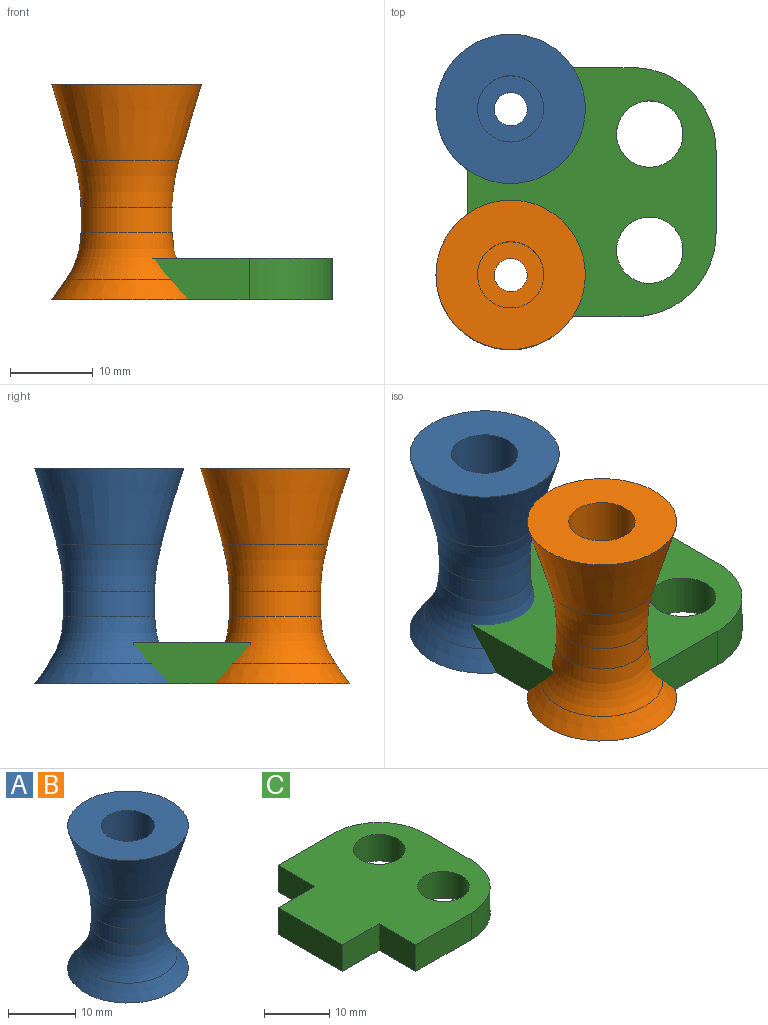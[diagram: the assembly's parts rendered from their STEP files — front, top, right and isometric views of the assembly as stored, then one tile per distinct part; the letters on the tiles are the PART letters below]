
ASSEMBLY  parts=3 mates=2
PART A: 10 faces, bbox 24.5x24.5x26 mm
  f0: cone r=5.5mm half-angle=16.3deg, axis (0,0,1), area 463.5mm2, adj f1,f9
  f1: plane 18x18mm, normal (0,0,1), area 204.2mm2, adj f0,f2
  f2: cylinder r=4mm len=18mm, axis (0,0,-1), area 452.4mm2, adj f1,f3
  f3: plane 8x8mm, normal (0,0,1), area 37.7mm2, adj f2,f4
  f4: cylinder r=2mm len=8mm, axis (0,0,-1), area 100.5mm2, adj f3,f5
  f5: plane 18x18mm, normal (0,0,-1), area 241.9mm2, adj f4,f6
  f6: cone r=9mm half-angle=35deg, axis (0,0,-1), area 151.2mm2, adj f5,f8
  f7: cylinder r=5.5mm len=11mm, axis (0,0,-1), area 103.3mm2, adj f8,f9
  f8: torus R=15.5mm, axis (0,0,-1), area 234.5mm2, adj f6,f7
  f9: torus R=25.5mm, axis (0,0,-1), area 205.7mm2, adj f0,f7
PART B: same geometry as A
PART C: 14 faces, bbox 30x30x5 mm
  f0: plane 12x5mm, normal (0,1,0), area 60mm2, adj f3,f4,f9,f13
  f1: plane 14x5mm, normal (-1,0,0), area 70mm2, adj f3,f4,f10,f12
  f2: plane 12x5mm, normal (0,-1,0), area 60mm2, adj f3,f4,f8,f11
  f3: plane 30x30mm, normal (0,0,1), area 628.5mm2, adj f0,f1,f2,f5,f6,f7,f8,f9
  f4: plane 30x30mm, normal (0,0,-1), area 628.5mm2, adj f0,f1,f2,f5,f6,f7,f8,f9
  f5: plane 10x5mm, normal (1,0,0), area 50mm2, adj f3,f4,f8,f9
  f6: cylinder r=4mm len=8mm, axis (0,0,1), area 125.7mm2, adj f3,f4
  f7: cylinder r=4mm len=8mm, axis (0,0,1), area 125.7mm2, adj f3,f4
  f8: cylinder r=10mm len=10mm, axis (0,0,1), area 78.5mm2, adj f2,f3,f4,f5
  f9: cylinder r=10mm len=10mm, axis (0,0,-1), area 78.5mm2, adj f0,f3,f4,f5
  f10: plane 8x5mm, normal (0,-1,0), area 40mm2, adj f1,f3,f4,f11
  f11: plane 8x5mm, normal (-1,0,0), area 40mm2, adj f2,f3,f4,f10
  f12: plane 8x5mm, normal (0,1,0), area 40mm2, adj f1,f3,f4,f13
  f13: plane 8x5mm, normal (-1,0,0), area 40mm2, adj f0,f3,f4,f12
PLACE A t=(45.35,45.38,19.78)mm
PLACE B t=(45.35,25.38,19.78)mm
PLACE C t=(55.1,35.38,19.78)mm
MATE fastened A.f0 <-> B.f1  axis (0,0,1) through (45.35,45.38,45.78)mm
MATE fastened B.f0 <-> C.f4  axis (0,0,-1) through (45.35,25.38,19.78)mm
